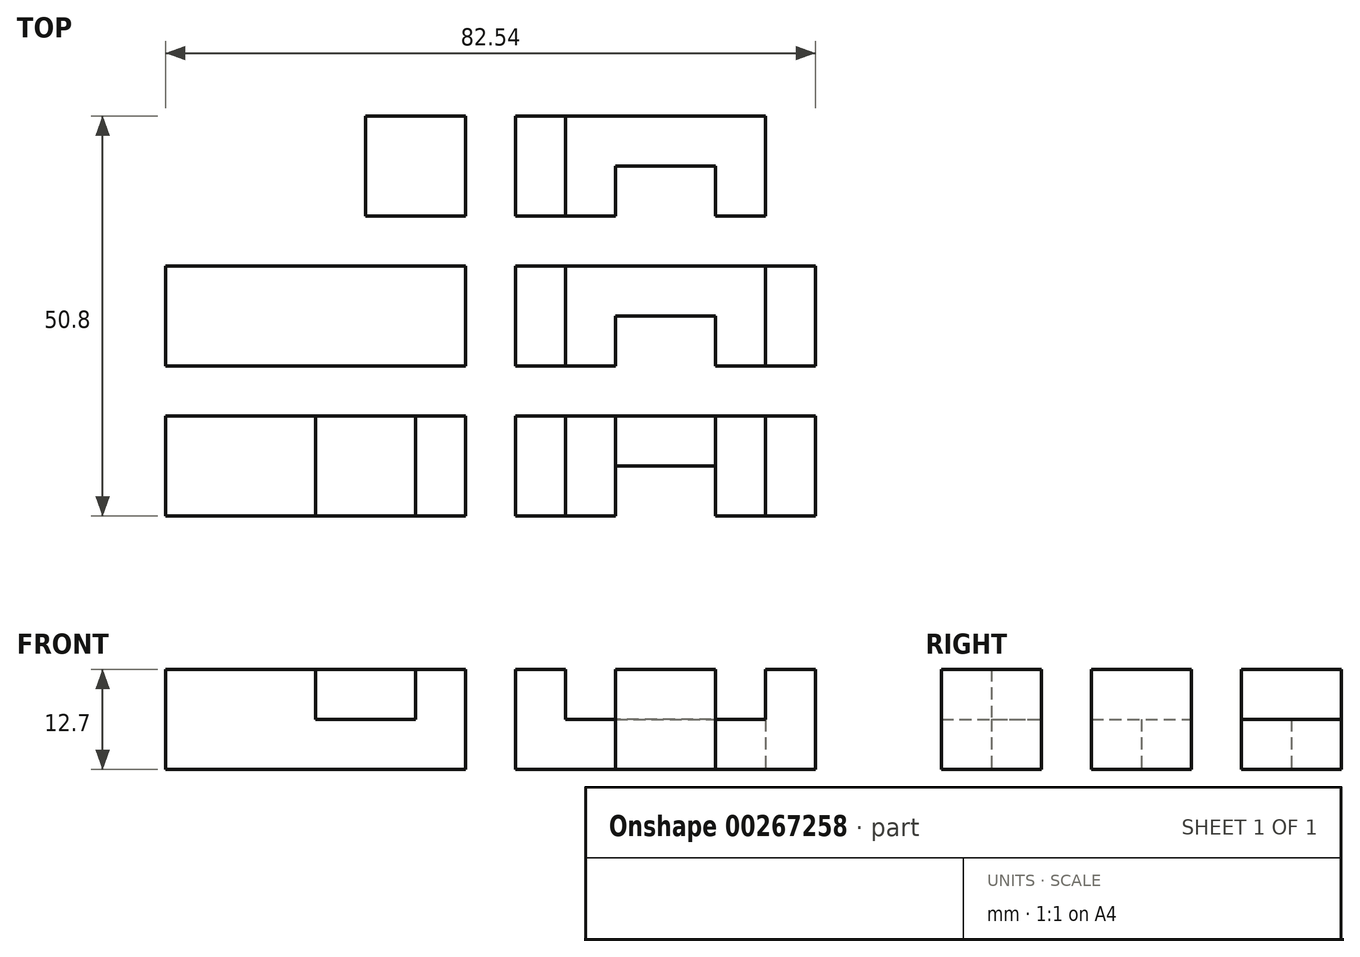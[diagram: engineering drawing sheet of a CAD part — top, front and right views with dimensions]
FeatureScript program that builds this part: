
annotation { "Feature Type Name" : "Feature", "Feature Type Description" : "" }
export const myFeature = defineFeature(function(context is Context, id is Id, definition is map)
    precondition{}
    {
        {
            var Q0;
            Q0=qCreatedBy(makeId("Top.planeOp"),FACE);
            var sketch = newSketch(context, id + "F0", { "sketchPlane" : qUnion([Q0])});
            skLineSegment(sketch, "E0.bottom", {"start": v(41.28, -25.4) * mm, "end": v(28.57, -25.4) * mm});
            skLineSegment(sketch, "E0.top", {"start": v(41.28, 25.4) * mm, "end": v(3.18, 25.4) * mm});
            skLineSegment(sketch, "E0.left", {"start": v(41.28, -25.4) * mm, "end": v(41.28, -12.7) * mm});
            skLineSegment(sketch, "E0.right", {"start": v(-41.28, -25.4) * mm, "end": v(-41.28, -12.7) * mm});
            skPoint(sketch, "E0.middle", {"position": v(0, 0) * mm});
            skLineSegment(sketch, "E1.bottom", {"start": v(41.27, -6.35) * mm, "end": v(28.57, -6.35) * mm});
            skLineSegment(sketch, "E1.top", {"start": v(41.27, 6.35) * mm, "end": v(3.18, 6.35) * mm});
            skLineSegment(sketch, "E1.left", {"start": v(41.28, -6.35) * mm, "end": v(41.28, 6.35) * mm});
            skLineSegment(sketch, "E1.right", {"start": v(-41.28, -6.35) * mm, "end": v(-41.28, 6.35) * mm});
            skLineSegment(sketch, "E2.bottom", {"start": v(-41.28, 25.4) * mm, "end": v(-3.18, 25.4) * mm});
            skLineSegment(sketch, "E2.top", {"start": v(-41.28, 12.7) * mm, "end": v(-3.18, 12.7) * mm});
            skLineSegment(sketch, "E2.left", {"start": v(-41.28, 25.4) * mm, "end": v(-41.28, 12.7) * mm});
            skLineSegment(sketch, "E2.right", {"start": v(-3.18, 25.4) * mm, "end": v(-3.18, 12.7) * mm});
            skLineSegment(sketch, "E3.bottom", {"start": v(28.57, 25.4) * mm, "end": v(3.18, 25.4) * mm});
            skLineSegment(sketch, "E3.top", {"start": v(41.28, 12.7) * mm, "end": v(28.57, 12.7) * mm});
            skLineSegment(sketch, "E3.left", {"start": v(41.28, 25.4) * mm, "end": v(41.28, 12.7) * mm});
            skLineSegment(sketch, "E3.right", {"start": v(3.18, 25.4) * mm, "end": v(3.18, 12.7) * mm});
            skLineSegment(sketch, "E4.bottom", {"start": v(-41.28, -25.4) * mm, "end": v(-22.23, -25.4) * mm});
            skLineSegment(sketch, "E4.top", {"start": v(-41.28, -12.7) * mm, "end": v(-3.18, -12.7) * mm});
            skLineSegment(sketch, "E4.right", {"start": v(-3.18, -25.4) * mm, "end": v(-3.18, -12.7) * mm});
            skLineSegment(sketch, "E5.top", {"start": v(41.28, -12.7) * mm, "end": v(3.18, -12.7) * mm});
            skLineSegment(sketch, "E5.right", {"start": v(3.18, -25.4) * mm, "end": v(3.18, -12.7) * mm});
            skLineSegment(sketch, "E6.left", {"start": v(-3.18, 6.35) * mm, "end": v(-3.18, -6.35) * mm});
            skLineSegment(sketch, "E6.right", {"start": v(3.18, 6.35) * mm, "end": v(3.18, -6.35) * mm});
            skLineSegment(sketch, "E7.trimOffspring", {"start": v(-3.18, -6.35) * mm, "end": v(-41.27, -6.35) * mm});
            skLineSegment(sketch, "E8.trimOffspring", {"start": v(-3.18, -25.4) * mm, "end": v(-41.28, -25.4) * mm});
            skLineSegment(sketch, "E9.trimOffspring", {"start": v(-3.18, 6.35) * mm, "end": v(-41.27, 6.35) * mm});
            skLineSegment(sketch, "E10.trimOffspring", {"start": v(-3.18, 25.4) * mm, "end": v(-28.57, 25.4) * mm});
            skLineSegment(sketch, "E11.top", {"start": v(-41.28, 25.4) * mm, "end": v(-28.57, 25.4) * mm});
            skLineSegment(sketch, "E11.left", {"start": v(-41.28, 12.7) * mm, "end": v(-41.28, 25.4) * mm});
            skLineSegment(sketch, "E11.right", {"start": v(-28.57, 12.7) * mm, "end": v(-28.57, 25.4) * mm});
            skLineSegment(sketch, "E12.bottom", {"start": v(-28.57, 12.7) * mm, "end": v(-15.87, 12.7) * mm});
            skLineSegment(sketch, "E12.top", {"start": v(-28.57, 25.4) * mm, "end": v(-15.87, 25.4) * mm});
            skLineSegment(sketch, "E12.right", {"start": v(-15.87, 12.7) * mm, "end": v(-15.87, 25.4) * mm});
            skLineSegment(sketch, "E13.bottom", {"start": v(-3.18, -6.35) * mm, "end": v(-22.22, -6.35) * mm});
            skLineSegment(sketch, "E13.right", {"start": v(-22.22, -6.35) * mm, "end": v(-22.23, 6.35) * mm});
            skLineSegment(sketch, "E14", {"start": v(-22.22, -12.7) * mm, "end": v(-22.23, -25.4) * mm});
            skLineSegment(sketch, "E15.bottom", {"start": v(-22.23, -25.4) * mm, "end": v(-9.53, -25.4) * mm});
            skLineSegment(sketch, "E15.top", {"start": v(-22.23, -12.7) * mm, "end": v(-9.53, -12.7) * mm});
            skLineSegment(sketch, "E15.right", {"start": v(-9.53, -25.4) * mm, "end": v(-9.53, -12.7) * mm});
            skLineSegment(sketch, "E16", {"start": v(-9.53, -6.35) * mm, "end": v(-9.53, 6.35) * mm});
            skLineSegment(sketch, "E17.trimOffspring", {"start": v(-9.53, -25.4) * mm, "end": v(-3.18, -25.4) * mm});
            skLineSegment(sketch, "E18.right", {"start": v(15.88, -25.4) * mm, "end": v(15.88, -12.7) * mm});
            skLineSegment(sketch, "E19.trimOffspring", {"start": v(15.88, -6.35) * mm, "end": v(15.88, 0) * mm});
            skLineSegment(sketch, "E20.trimOffspring", {"start": v(15.88, 12.7) * mm, "end": v(15.88, 19.05) * mm});
            skLineSegment(sketch, "E21.top", {"start": v(41.28, 25.4) * mm, "end": v(28.57, 25.4) * mm});
            skLineSegment(sketch, "E21.right", {"start": v(28.57, -25.4) * mm, "end": v(28.57, -12.7) * mm});
            skLineSegment(sketch, "E22.trimOffspring", {"start": v(41.28, 12.7) * mm, "end": v(41.28, 25.4) * mm});
            skLineSegment(sketch, "E23.trimOffspring", {"start": v(28.57, 12.7) * mm, "end": v(28.57, 19.05) * mm});
            skLineSegment(sketch, "E24.trimOffspring", {"start": v(28.57, -6.35) * mm, "end": v(28.57, 0) * mm});
            skLineSegment(sketch, "E25", {"start": v(15.88, 19.05) * mm, "end": v(28.57, 19.05) * mm});
            skLineSegment(sketch, "E26", {"start": v(15.88, 0) * mm, "end": v(28.57, 0) * mm});
            skLineSegment(sketch, "E27", {"start": v(15.88, -19.05) * mm, "end": v(28.57, -19.05) * mm});
            skLineSegment(sketch, "E28.trimOffspring", {"start": v(15.87, -6.35) * mm, "end": v(3.18, -6.35) * mm});
            skLineSegment(sketch, "E29.trimOffspring", {"start": v(15.88, -25.4) * mm, "end": v(3.18, -25.4) * mm});
            skLineSegment(sketch, "E30.trimOffspring", {"start": v(15.88, 12.7) * mm, "end": v(3.18, 12.7) * mm});
            skLineSegment(sketch, "E31", {"start": v(9.53, -25.4) * mm, "end": v(9.53, -12.7) * mm});
            skLineSegment(sketch, "E32", {"start": v(34.92, -25.4) * mm, "end": v(34.92, -12.7) * mm});
            skPoint(sketch, "E33.orphan", {"position": v(15.88, 25.4) * mm});
            skPoint(sketch, "E34.orphan", {"position": v(28.57, 6.35) * mm});
            skPoint(sketch, "E35.orphan", {"position": v(15.88, 6.35) * mm});
            skLineSegment(sketch, "E36.trimOffspring", {"start": v(9.53, 12.7) * mm, "end": v(9.53, 25.4) * mm});
            skLineSegment(sketch, "E37.trimOffspring", {"start": v(34.92, 12.7) * mm, "end": v(34.92, 25.4) * mm});
            skLineSegment(sketch, "E38.trimOffspring", {"start": v(34.92, -6.35) * mm, "end": v(34.92, 6.35) * mm});
            skLineSegment(sketch, "E39.trimOffspring", {"start": v(9.53, -6.35) * mm, "end": v(9.53, 6.35) * mm});
            skSolve(sketch);
        }
        {
            var Q0;
            Q0=makeQuery(id+"F0.imprint","IMPRINT",FACE,{"disambiguationData":[TD([[makeQuery(id+"F0.imprint","IMPRINT",EDGE,{"derivedFrom":sQuery(id+"F0.wireOp",EDGE,"E11.top")}),-1.0]])]});
            var Q1;
            {var subQ0=sQuery(id+"F0.wireOp",EDGE,"E2.right");Q1=makeQuery(id+"F0.imprint","IMPRINT",FACE,{"disambiguationData":[TD([[makeQuery(id+"F0.imprint","IMPRINT",EDGE,{"derivedFrom":subQ0}),-1.0]])]});}
            var Q2;
            Q2=makeQuery(id+"F0.imprint","IMPRINT",FACE,{"disambiguationData":[TD([[makeQuery(id+"F0.imprint","IMPRINT",EDGE,{"derivedFrom":sQuery(id+"F0.wireOp",EDGE,"E7.trimOffspring")}),-1.0]])]});
            var Q3;
            {var subQ0=sQuery(id+"F0.wireOp",EDGE,"E6.left");Q3=makeQuery(id+"F0.imprint","IMPRINT",FACE,{"disambiguationData":[TD([[makeQuery(id+"F0.imprint","IMPRINT",EDGE,{"derivedFrom":subQ0}),-1.0]])]});}
            var Q4;
            {var subQ0=sQuery(id+"F0.wireOp",EDGE,"E4.right");Q4=makeQuery(id+"F0.imprint","IMPRINT",FACE,{"disambiguationData":[TD([[makeQuery(id+"F0.imprint","IMPRINT",EDGE,{"derivedFrom":subQ0}),1.0]])]});}
            var Q5;
            {var subQ0=sQuery(id+"F0.wireOp",EDGE,"E0.right");Q5=makeQuery(id+"F0.imprint","IMPRINT",FACE,{"disambiguationData":[TD([[makeQuery(id+"F0.imprint","IMPRINT",EDGE,{"derivedFrom":subQ0}),-1.0]])]});}
            var Q6;
            {var subQ0=sQuery(id+"F0.wireOp",EDGE,"E5.right");Q6=makeQuery(id+"F0.imprint","IMPRINT",FACE,{"disambiguationData":[TD([[makeQuery(id+"F0.imprint","IMPRINT",EDGE,{"derivedFrom":subQ0}),-1.0]])]});}
            var Q7;
            {var subQ5=sQuery(id+"F0.wireOp",EDGE,"E27");Q7=makeQuery(id+"F0.imprint","IMPRINT",FACE,{"disambiguationData":[TD([[makeQuery(id+"F0.imprint","IMPRINT",EDGE,{"derivedFrom":subQ5}),1.0]])]});}
            var Q8;
            {var subQ0=sQuery(id+"F0.wireOp",EDGE,"E0.left");Q8=makeQuery(id+"F0.imprint","IMPRINT",FACE,{"disambiguationData":[TD([[makeQuery(id+"F0.imprint","IMPRINT",EDGE,{"derivedFrom":subQ0}),1.0]])]});}
            var Q9;
            {var subQ0=sQuery(id+"F0.wireOp",EDGE,"E1.left");Q9=makeQuery(id+"F0.imprint","IMPRINT",FACE,{"disambiguationData":[TD([[makeQuery(id+"F0.imprint","IMPRINT",EDGE,{"derivedFrom":subQ0}),1.0]])]});}
            var Q10;
            {var subQ0=sQuery(id+"F0.wireOp",EDGE,"E6.right");Q10=makeQuery(id+"F0.imprint","IMPRINT",FACE,{"disambiguationData":[TD([[makeQuery(id+"F0.imprint","IMPRINT",EDGE,{"derivedFrom":subQ0}),1.0]])]});}
            var Q11;
            {var subQ0=sQuery(id+"F0.wireOp",EDGE,"E3.right");Q11=makeQuery(id+"F0.imprint","IMPRINT",FACE,{"disambiguationData":[TD([[makeQuery(id+"F0.imprint","IMPRINT",EDGE,{"derivedFrom":subQ0}),1.0]])]});}
            var Q12;
            {var subQ0=sQuery(id+"F0.wireOp",EDGE,"E22.trimOffspring");Q12=makeQuery(id+"F0.imprint","IMPRINT",FACE,{"disambiguationData":[TD([[makeQuery(id+"F0.imprint","IMPRINT",EDGE,{"derivedFrom":subQ0}),1.0]])]});}
            extrude(context, id + "F1", {"entities" : qUnion([Q0, Q1, Q2, Q3, Q4, Q5, Q6, Q7, Q8, Q9, Q10, Q11, Q12]), "depth" : 12.7 * mm});
        }
        {
            var Q0;
            Q0=makeQuery(id+"F0.imprint","IMPRINT",FACE,{"disambiguationData":[TD([[makeQuery(id+"F0.imprint","IMPRINT",EDGE,{"derivedFrom":sQuery(id+"F0.wireOp",EDGE,"E12.bottom")}),1.0]])]});
            var Q1;
            {var subQ0=sQuery(id+"F0.wireOp",EDGE,"E13.right");Q1=makeQuery(id+"F0.imprint","IMPRINT",FACE,{"disambiguationData":[TD([[makeQuery(id+"F0.imprint","IMPRINT",EDGE,{"derivedFrom":subQ0}),-1.0]])]});}
            var Q2;
            {var subQ3=sQuery(id+"F0.wireOp",EDGE,"E31");Q2=makeQuery(id+"F0.imprint","IMPRINT",FACE,{"disambiguationData":[TD([[makeQuery(id+"F0.imprint","IMPRINT",EDGE,{"derivedFrom":subQ3}),-1.0]])]});}
            var Q3;
            {var subQ1=sQuery(id+"F0.wireOp",EDGE,"E19.trimOffspring");Q3=makeQuery(id+"F0.imprint","IMPRINT",FACE,{"disambiguationData":[TD([[makeQuery(id+"F0.imprint","IMPRINT",EDGE,{"derivedFrom":subQ1}),1.0]])]});}
            var Q4;
            {var subQ4=sQuery(id+"F0.wireOp",EDGE,"E20.trimOffspring");Q4=makeQuery(id+"F0.imprint","IMPRINT",FACE,{"disambiguationData":[TD([[makeQuery(id+"F0.imprint","IMPRINT",EDGE,{"derivedFrom":subQ4}),1.0]])]});}
            var Q5;
            {var subQ4=sQuery(id+"F0.wireOp",EDGE,"E32");Q5=makeQuery(id+"F0.imprint","IMPRINT",FACE,{"disambiguationData":[TD([[makeQuery(id+"F0.imprint","IMPRINT",EDGE,{"derivedFrom":subQ4}),1.0]])]});}
            var Q6;
            Q6=makeQuery(id+"F0.imprint","IMPRINT",FACE,{"disambiguationData":[TD([[makeQuery(id+"F0.imprint","IMPRINT",EDGE,{"derivedFrom":sQuery(id+"F0.wireOp",EDGE,"E14")}),1.0]])]});
            extrude(context, id + "F2", {"entities" : qUnion([Q0, Q1, Q2, Q3, Q4, Q5, Q6]), "operationType" : NewBodyOperationType.ADD, "depth" : 6.35 * mm});
        }
    });
